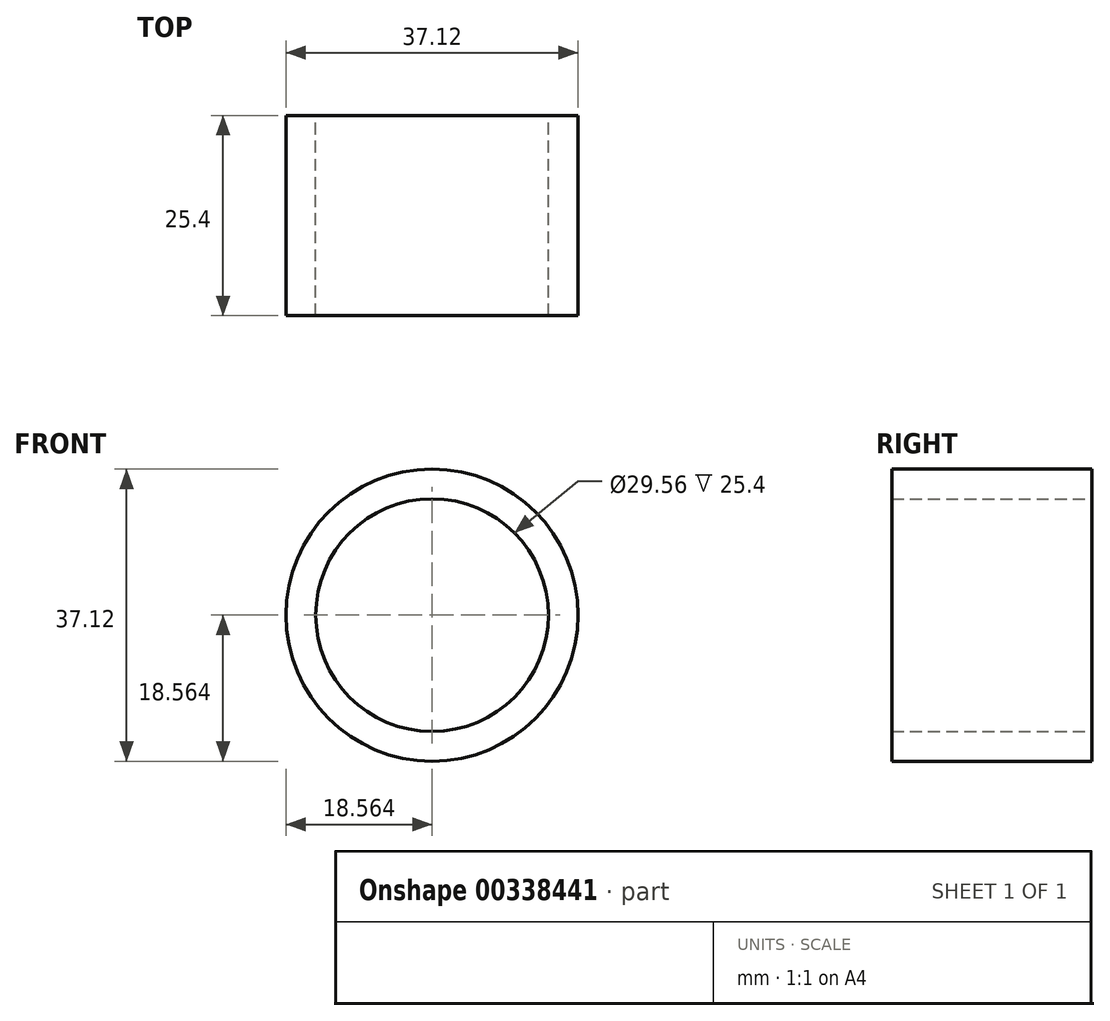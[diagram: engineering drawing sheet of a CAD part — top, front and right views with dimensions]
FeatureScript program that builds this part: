
annotation { "Feature Type Name" : "Feature", "Feature Type Description" : "" }
export const myFeature = defineFeature(function(context is Context, id is Id, definition is map)
    precondition{}
    {
        {
            var Q0;
            Q0=qCreatedBy(makeId("Front.planeOp"),FACE);
            var sketch = newSketch(context, id + "F0", { "sketchPlane" : qUnion([Q0])});
            skLineSegment(sketch, "E0.bottom", {"start": v(0, 28.64) * mm, "end": v(63.27, 28.64) * mm});
            skLineSegment(sketch, "E0.top", {"start": v(0, 0) * mm, "end": v(63.27, 0) * mm});
            skLineSegment(sketch, "E0.left", {"start": v(0, 28.64) * mm, "end": v(0, 0) * mm});
            skLineSegment(sketch, "E0.right", {"start": v(63.27, 28.64) * mm, "end": v(63.27, 0) * mm});
            skPoint(sketch, "E1.first.point", {"position": v(42.17, 17.64) * mm});
            skPoint(sketch, "E1.second.point", {"position": v(46.9, 11.32) * mm});
            skPoint(sketch, "E1.third.point", {"position": v(42.81, 10.04) * mm});
            skPoint(sketch, "E2.first.point", {"position": v(54.98, 13.65) * mm});
            skPoint(sketch, "E2.second.point", {"position": v(48.34, 10.04) * mm});
            skPoint(sketch, "E2.third.point", {"position": v(50.28, 15.82) * mm});
            skPoint(sketch, "E3.first.point", {"position": v(32.41, -6.44) * mm});
            skPoint(sketch, "E3.second.point", {"position": v(1.93, 12.6) * mm});
            skPoint(sketch, "E3.third.point", {"position": v(32.9, -2.12) * mm});
            skCircle(sketch, "E4", {"center": v(32.9, -2.12) * mm, "radius": 18.56 * mm});
            skCircle(sketch, "E5", {"center": v(32.9, -2.12) * mm, "radius": 14.78 * mm});
            skSolve(sketch);
        }
        {
            var Q0;
            {var subQ0=sQuery(id+"F0.wireOp",EDGE,"E4");var subQ1=sQuery(id+"F0.wireOp",EDGE,"E0.top");var subQ2=makeQuery(id+"F0.imprint","INTERSECT",VERTEX,{"disambiguationData":[OD(0.0)],"derivedFrom":[subQ1,subQ0]});Q0=makeQuery(id+"F0.imprint","IMPRINT",FACE,{"disambiguationData":[TD([[makeQuery(id+"F0.imprint","IMPRINT",EDGE,{"disambiguationData":[TD([[subQ2,-1.0]])],"derivedFrom":subQ1}),-1.0]])]});}
            extrude(context, id + "F1", {"entities" : qUnion([Q0]), "depth" : 25.4 * mm});
        }
        {
            var Q0;
            {var subQ0=sQuery(id+"F0.wireOp",EDGE,"E4");var subQ1=sQuery(id+"F0.wireOp",EDGE,"E0.top");var subQ2=makeQuery(id+"F0.imprint","INTERSECT",VERTEX,{"disambiguationData":[OD(0.0)],"derivedFrom":[subQ1,subQ0]});Q0=makeQuery(id+"F0.imprint","IMPRINT",FACE,{"disambiguationData":[TD([[makeQuery(id+"F0.imprint","IMPRINT",EDGE,{"disambiguationData":[TD([[subQ2,-1.0]])],"derivedFrom":subQ1}),1.0]])]});}
            extrude(context, id + "F2", {"entities" : qUnion([Q0]), "operationType" : NewBodyOperationType.ADD, "depth" : 25.4 * mm});
        }
    });
